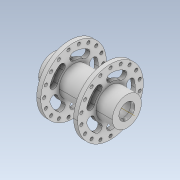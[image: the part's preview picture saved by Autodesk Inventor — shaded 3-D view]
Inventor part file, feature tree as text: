
AUTODESK INVENTOR PART (.ipt)
format: ipt  version: 2021 (Build 250183000, 183)  size: 449,024 bytes
history: native  units: mm
features: other x5, revolve x2, sketch x2, pattern_circular x1, mirror x1
ambient origin geometry x8: Origin, YZ Plane, XZ Plane, XY Plane, X Axis, Y Axis, Z Axis, Center Point
bodies: Body1 (feature_tree), Body2 (feature_tree)
feature tree (11):
  other  "LlantaUser Library-Bike Weell.ipt"
  revolve  "Revolución1"  [1 undecoded]
  revolve  "Revolución3"  [1 undecoded]
  pattern_circular  "Patrón circular2"  Angle=90.0deg  [1 undecoded]
  mirror  "Simetría1"
  other  "Solid1::LlantaUser Library-Bike Weell.ipt"
  other  "OperaciónIdentificador1"
  sketch  "Boceto1"  dims[d0=10.0mm d1=5.0mm]
  sketch  "Boceto3"  dims[d2=5.0mm d3=3.0mm d4=90.0deg d5=4.0mm d10=90.0deg d11=60.0mm d12=360.0deg]
  other  "Sólido3"
  other  "Sólido1"
note: 3 required parameter values undecoded (feature->parameter linkage not recoverable at this tier; creation-order binding heuristic only, values carry confidence <= 0.55)